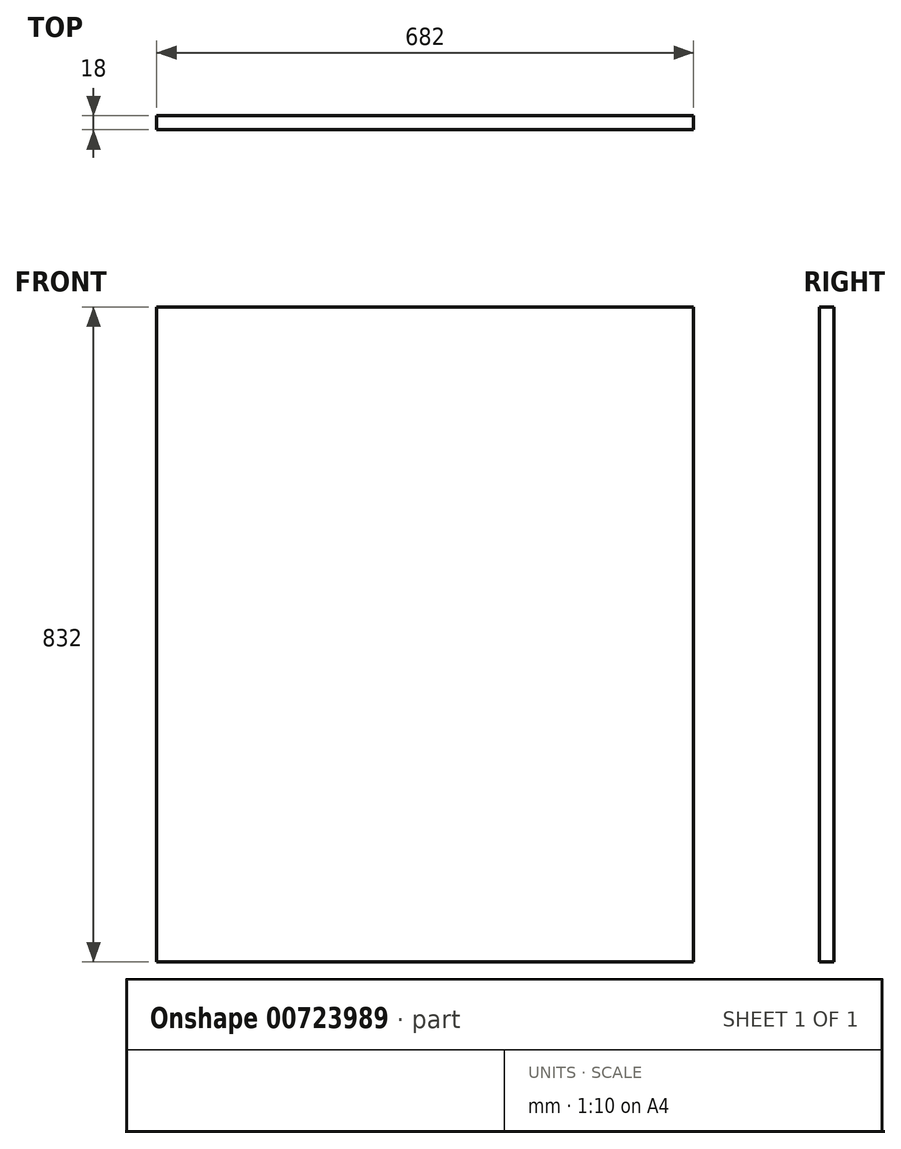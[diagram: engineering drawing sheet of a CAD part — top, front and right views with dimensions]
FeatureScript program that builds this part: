
annotation { "Feature Type Name" : "Feature", "Feature Type Description" : "" }
export const myFeature = defineFeature(function(context is Context, id is Id, definition is map)
    precondition{}
    {
        {
            var Q0;
            Q0=qCreatedBy(makeId("Front.planeOp"),FACE);
            var sketch = newSketch(context, id + "F0", { "sketchPlane" : qUnion([Q0])});
            skLineSegment(sketch, "E0.bottom", {"start": v(-341, 416) * mm, "end": v(341, 416) * mm});
            skLineSegment(sketch, "E0.top", {"start": v(-341, -416) * mm, "end": v(341, -416) * mm});
            skLineSegment(sketch, "E0.left", {"start": v(-341, 416) * mm, "end": v(-341, -416) * mm});
            skLineSegment(sketch, "E0.right", {"start": v(341, 416) * mm, "end": v(341, -416) * mm});
            skLineSegment(sketch, "E1", {"start": v(-341, 416) * mm, "end": v(341, -416) * mm, "construction": true});
            skLineSegment(sketch, "E2", {"start": v(341, 416) * mm, "end": v(-341, -416) * mm, "construction": true});
            skSolve(sketch);
        }
        {
            var Q0;
            Q0=qSketchRegion(id+"F0",true);
            extrude(context, id + "F1", {"entities" : qUnion([Q0]), "depth" : 18 * mm, "offsetDistance" : 25 * mm});
        }
    });
